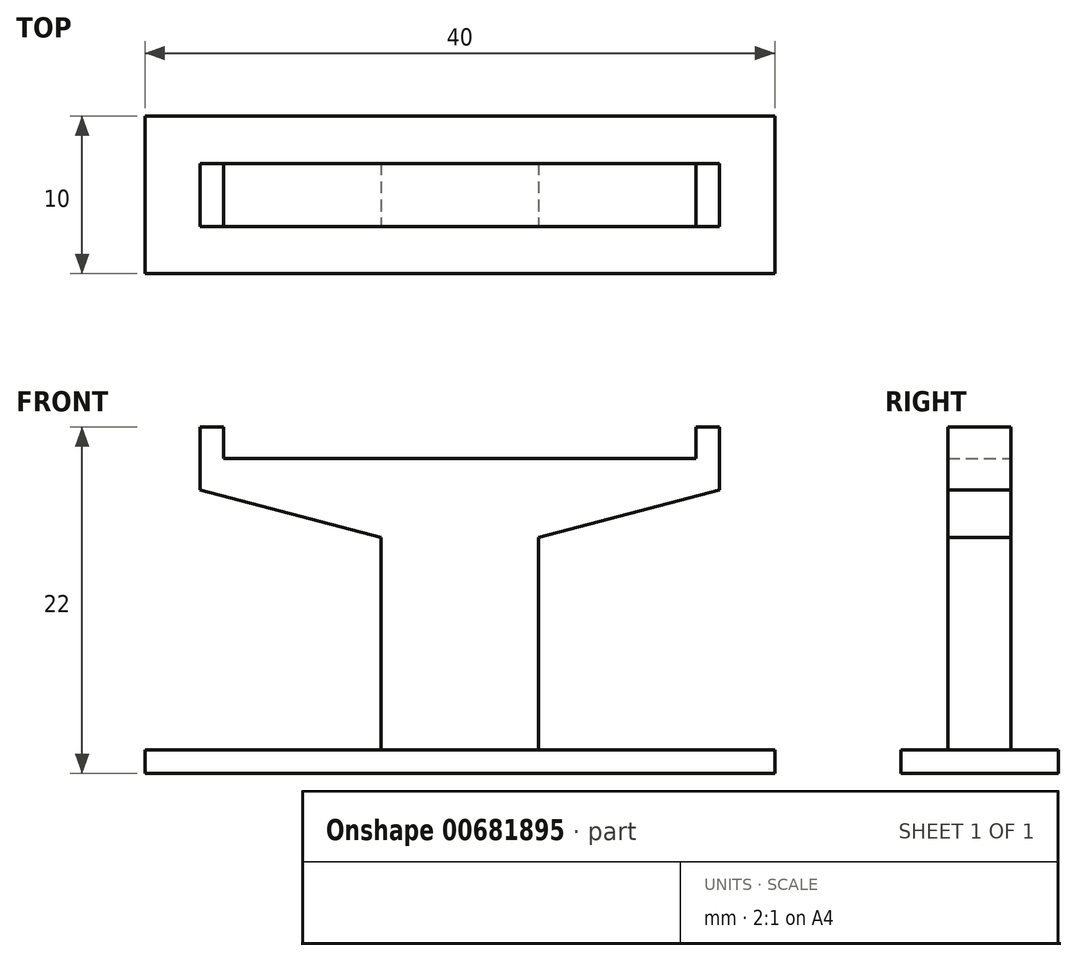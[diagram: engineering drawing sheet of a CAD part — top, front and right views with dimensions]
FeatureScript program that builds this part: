
annotation { "Feature Type Name" : "Feature", "Feature Type Description" : "" }
export const myFeature = defineFeature(function(context is Context, id is Id, definition is map)
    precondition{}
    {
        {
            assignVariable(context, id + "F0", {"name" : "height", "anyValue" : 20});
        }
        {
            assignVariable(context, id + "F1", {"name" : "width", "anyValue" : 33});
        }
        {
            assignVariable(context, id + "F2", {"name" : "track_width", "anyValue" : 30});
        }
        {
            assignVariable(context, id + "F3", {"name" : "track_height", "anyValue" : 2});
        }
        {
            var Q0;
            Q0=qCreatedBy(makeId("Top.planeOp"),FACE);
            var sketch = newSketch(context, id + "F4", { "sketchPlane" : qUnion([Q0])});
            skLineSegment(sketch, "E0.bottom", {"start": v(20, -5) * mm, "end": v(-20, -5) * mm});
            skLineSegment(sketch, "E0.top", {"start": v(20, 5) * mm, "end": v(-20, 5) * mm});
            skLineSegment(sketch, "E0.left", {"start": v(20, -5) * mm, "end": v(20, 5) * mm});
            skLineSegment(sketch, "E0.right", {"start": v(-20, -5) * mm, "end": v(-20, 5) * mm});
            skPoint(sketch, "E0.middle", {"position": v(0, 0) * mm});
            skLineSegment(sketch, "E1.bottom", {"start": v(-5, 2) * mm, "end": v(5, 2) * mm});
            skLineSegment(sketch, "E1.top", {"start": v(-5, -2) * mm, "end": v(5, -2) * mm});
            skLineSegment(sketch, "E1.left", {"start": v(-5, 2) * mm, "end": v(-5, -2) * mm});
            skLineSegment(sketch, "E1.right", {"start": v(5, 2) * mm, "end": v(5, -2) * mm});
            skSolve(sketch);
        }
        {
            var Q0;
            Q0=qSketchRegion(id+"F4",true);
            var Q1;
            {var subQ0=sQuery(id+"F4.wireOp",EDGE,"E0.right");Q1=makeQuery(id+"F4.imprint","IMPRINT",FACE,{"disambiguationData":[TD([[makeQuery(id+"F4.imprint","IMPRINT",EDGE,{"derivedFrom":subQ0}),-1.0]])]});}
            extrude(context, id + "F5", {"entities" : qUnion([Q0, Q1]), "depth" : 1.5 * mm, "offsetDistance" : 25 * mm});
        }
        {
            var Q0;
            Q0=makeQuery(id+"F4.imprint","IMPRINT",FACE,{"disambiguationData":[TD([[makeQuery(id+"F4.imprint","IMPRINT",EDGE,{"derivedFrom":sQuery(id+"F4.wireOp",EDGE,"E1.bottom")}),-1.0]])]});
            extrude(context, id + "F6", {"entities" : qUnion([Q0]), "operationType" : NewBodyOperationType.ADD, "depth" : (getVariable(context, 'height')) * mm, "offsetDistance" : 25 * mm});
        }
        {
            var Q0;
            Q0=makeQuery(id+"F6.opExtrude","CAP_FACE",FACE,{"disambiguationData":[OSD([sQuery(id+"F4.wireOp",EDGE,"E1.bottom"),sQuery(id+"F4.wireOp",EDGE,"E1.top"),sQuery(id+"F4.wireOp",EDGE,"E1.left"),sQuery(id+"F4.wireOp",EDGE,"E1.right")])],"isStart":false});
            var sketch = newSketch(context, id + "F7", { "sketchPlane" : qUnion([Q0])});
            skLineSegment(sketch, "E2.bottom", {"start": v(-16.5, 2) * mm, "end": v(16.5, 2) * mm});
            skLineSegment(sketch, "E2.top", {"start": v(-16.5, -2) * mm, "end": v(16.5, -2) * mm});
            skLineSegment(sketch, "E2.left", {"start": v(-16.5, 2) * mm, "end": v(-16.5, -2) * mm});
            skLineSegment(sketch, "E2.right", {"start": v(16.5, 2) * mm, "end": v(16.5, -2) * mm});
            skPoint(sketch, "E2.middle", {"position": v(0, 0) * mm});
            skSolve(sketch);
        }
        {
            var Q0;
            Q0=qSketchRegion(id+"F7",true);
            extrude(context, id + "F8", {"entities" : qUnion([Q0]), "operationType" : NewBodyOperationType.ADD, "depth" : -5 * mm, "offsetDistance" : 25 * mm});
        }
        {
            var Q0;
            Q0=makeQuery(id+"F8.opExtrude","CAP_EDGE",EDGE,{"disambiguationData":[OSD([sQuery(id+"F7.wireOp",EDGE,"E2.right")])],"isStart":false});
            chamfer(context, id + "F9", {"entities" : qUnion([Q0]), "chamferType" : ChamferType.TWO_OFFSETS, "width1" : ((getVariable(context, 'width') - (getVariable(context, 'track_width') / 3)) / 2) * mm, "oppositeDirection" : false, "width2" : 3 * mm, "tangentPropagation" : true});
        }
        {
            var Q0;
            Q0=makeQuery(id+"F8.opExtrude","CAP_EDGE",EDGE,{"disambiguationData":[OSD([sQuery(id+"F7.wireOp",EDGE,"E2.left")])],"isStart":false});
            chamfer(context, id + "F10", {"entities" : qUnion([Q0]), "chamferType" : ChamferType.TWO_OFFSETS, "width1" : 3 * mm, "oppositeDirection" : false, "width2" : ((getVariable(context, 'width') - (getVariable(context, 'track_width') / 3)) / 2) * mm, "tangentPropagation" : true});
        }
        {
            var Q0;
            Q0=makeQuery(id+"F8.boolean.opBoolean","MERGE",FACE,{"derivedFrom":[makeQuery(id+"F6.opExtrude","CAP_FACE",FACE,{"disambiguationData":[OSD([sQuery(id+"F4.wireOp",EDGE,"E1.bottom"),sQuery(id+"F4.wireOp",EDGE,"E1.top"),sQuery(id+"F4.wireOp",EDGE,"E1.left"),sQuery(id+"F4.wireOp",EDGE,"E1.right")])],"isStart":false}),makeQuery(id+"F8.opExtrude","CAP_FACE",FACE,{"disambiguationData":[OSD([sQuery(id+"F7.wireOp",EDGE,"E2.bottom"),sQuery(id+"F7.wireOp",EDGE,"E2.top"),sQuery(id+"F7.wireOp",EDGE,"E2.left"),sQuery(id+"F7.wireOp",EDGE,"E2.right")])],"isStart":true})]});
            var sketch = newSketch(context, id + "F11", { "sketchPlane" : qUnion([Q0])});
            skLineSegment(sketch, "E3.bottom", {"start": v(16.5, -2) * mm, "end": v(15, -2) * mm});
            skLineSegment(sketch, "E3.top", {"start": v(16.5, 2) * mm, "end": v(15, 2) * mm});
            skLineSegment(sketch, "E3.left", {"start": v(16.5, -2) * mm, "end": v(16.5, 2) * mm});
            skLineSegment(sketch, "E3.right", {"start": v(15, -2) * mm, "end": v(15, 2) * mm});
            skLineSegment(sketch, "E4.bottom", {"start": v(-16.5, -2) * mm, "end": v(-15, -2) * mm});
            skLineSegment(sketch, "E4.top", {"start": v(-16.5, 2) * mm, "end": v(-15, 2) * mm});
            skLineSegment(sketch, "E4.left", {"start": v(-16.5, -2) * mm, "end": v(-16.5, 2) * mm});
            skLineSegment(sketch, "E4.right", {"start": v(-15, -2) * mm, "end": v(-15, 2) * mm});
            skSolve(sketch);
        }
        {
            var Q0;
            Q0=makeQuery(id+"F11.imprint","IMPRINT",FACE,{"disambiguationData":[TD([[makeQuery(id+"F11.imprint","IMPRINT",EDGE,{"derivedFrom":sQuery(id+"F11.wireOp",EDGE,"E3.bottom")}),1.0]])]});
            var Q1;
            Q1=makeQuery(id+"F11.imprint","IMPRINT",FACE,{"disambiguationData":[TD([[makeQuery(id+"F11.imprint","IMPRINT",EDGE,{"derivedFrom":sQuery(id+"F11.wireOp",EDGE,"E4.bottom")}),1.0]])]});
            extrude(context, id + "F12", {"entities" : qUnion([Q0, Q1]), "operationType" : NewBodyOperationType.ADD, "depth" : (getVariable(context, 'track_height')) * mm, "offsetDistance" : 25 * mm});
        }
    });
